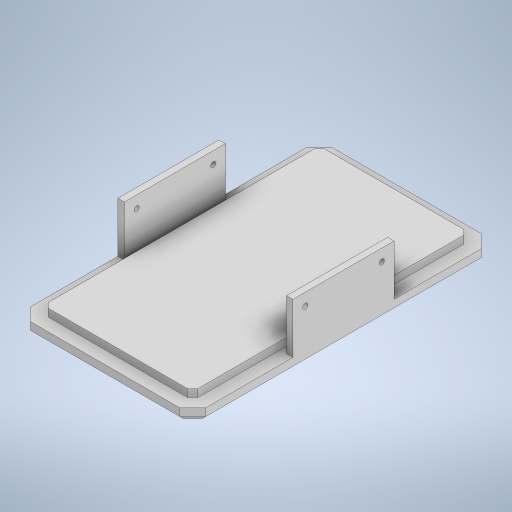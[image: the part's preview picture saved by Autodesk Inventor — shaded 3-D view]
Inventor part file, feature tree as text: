
AUTODESK INVENTOR PART (.ipt)
format: ipt  version: 2023 (Build 270158000, 158)  size: 285,696 bytes
history: native  units: mm
features: extrude x4, chamfer x3, sketch x2, other x1
ambient origin geometry x8: Origin, YZ Plane, XZ Plane, XY Plane, X Axis, Y Axis, Z Axis, Center Point
bodies: Body1 (feature_tree)
feature tree (10):
  other  "솔리드1"
  sketch  "스케치1"
  extrude  "돌출1"  Depth=58.6mm
  extrude  "돌출2"  Depth=108.2mm
  chamfer  "모따기1"  Distance=5.0mm
  extrude  "돌출3"  Depth=5.0mm TaperAngle=0.0deg
  extrude  "돌출4"  Depth=39.6mm
  chamfer  "모따기2"  Distance=19.7mm
  chamfer  "모따기3"  Distance=5.0mm Angle=45.0deg
  sketch  "스케치2"
